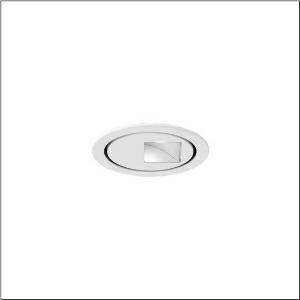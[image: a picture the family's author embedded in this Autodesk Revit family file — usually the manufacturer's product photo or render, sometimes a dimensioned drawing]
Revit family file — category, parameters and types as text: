
# Revit family: lunis_11_micro_round_51dj11cd1wm21
name_source: partatom
category: Lighting Fixtures
units: mm (PartAtom-declared; Revit-internal decimal feet)

## family parameters
Cut with Voids When Loaded = No
Host = Face
Light Source = No
Part Type = Normal
Room Calculation Point = No
Round Connector Dimension = Use Diameter
Shared = No

## types (1)
- Lunis 11 micro round (1 x LED 3000K / CRI = 90 (unbekannt), 1100 lm, 3000K)
    Apparent Load = 20 VA
    CIE Flux Codes = 42 75 96 100 100
    Color Rendering = 90
    Color Temperature = 3000K
    Default Elevation = 1800 mm
    Description = Lunis 11 micro round, downlight, light control with wallwasher, of highly reflective aluminium, highly specular, light emission: direct distribution, LED rated luminous flux: 1.100lm, light colour: 930, with terminal, 5-pole, mains connection: 220..230V, AC, 50/60Hz, LED module, of aluminium, highly specular, white, diameter: 114mm, clamping range: 1..40mm, recessing ring, of plastic, traffic white (RAL 9016), protection rating (complete): IP20, insulation class (complete): insulation class II (safety insulation), certification: CE, permissible ambient temperature for indoor applications: 0..+35°C, packaging unit: 1 piece
    Height = 0 mm  [stored 0 ft]
    Lamp = 1 x LED 3000K / CRI >= 90 (unbekannt)
    Lamp Light Flux = 1100 lm
    Lamp count = 1
    Length = 114 mm
    Luminous efficacy = 56 lm/W
    Manufacturer = Siteco
    ModVariant = No
    Model = 51DJ11CD1WM21
    Mounting Place = Ceiling
    Mounting Type = Recessed
    Number of Poles = 1
    OnlyDefault = Yes
    Power Factor = 1
    Product Name = Lunis 11 micro round
    Product group = downlight
    ProductGroupID = 400
    Protection Class = Protection class II
    Protection Degree = IP 20
    RLX_Detail_Level = 1
    RLX_Emergency_Light_Flux = 0 lm
    RLX_Emergency_Type = 0
    RLX_Emergency_Type_DB = No
    RlxData = <blob elided: 40557 chars, md5=9823c13b>
    Socket = socket
    Standby Power = 0 W
    System Light Flux = 1100 lm
    System Power = 20 W
    Type Comments = Product without accessories
    Type Image = l_1004773.jpg
    URL = http://relux.com
    VarID = ---
    Voltage = 0 V
    Weight = 0.00 kg
    Width = 114 mm

note: [stored X ft] marks values corroborated as IEEE doubles in the binary element streams (Revit-internal decimal feet)

## geometry (parser evidence)
native form markers: Blend x4, Sweep x9
no freeform markers — native parametric forms only
